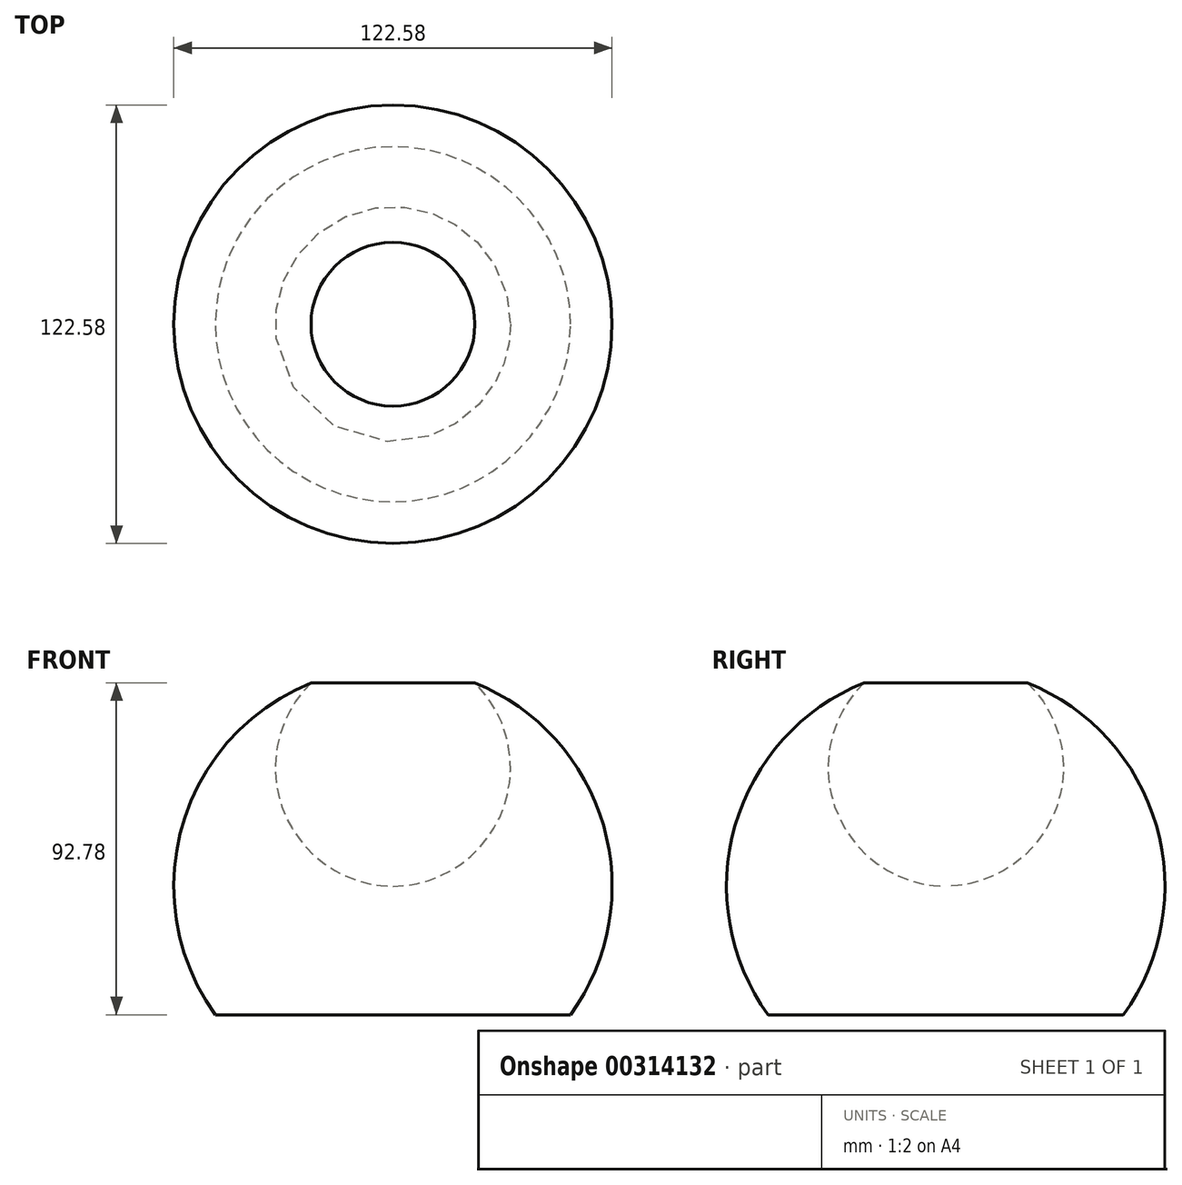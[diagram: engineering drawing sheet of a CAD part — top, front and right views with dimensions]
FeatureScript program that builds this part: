
annotation { "Feature Type Name" : "Feature", "Feature Type Description" : "" }
export const myFeature = defineFeature(function(context is Context, id is Id, definition is map)
    precondition{}
    {
        {
            var Q0;
            Q0=qCreatedBy(makeId("Front.planeOp"),FACE);
            var sketch = newSketch(context, id + "F0", { "sketchPlane" : qUnion([Q0])});
            skArc(sketch, "E0", {"start": v(49.65, -35.93) * mm, "mid": v(58.89, 16.98) * mm, "end": v(22.9, 56.85) * mm});
            skLineSegment(sketch, "E1", {"start": v(-49.65, -35.93) * mm, "end": v(49.65, -35.93) * mm});
            skLineSegment(sketch, "E2", {"start": v(0, -35.93) * mm, "end": v(0, 67.72) * mm});
            skArc(sketch, "E3", {"start": v(-23.82, 56.47) * mm, "mid": v(0, 0) * mm, "end": v(22.9, 56.85) * mm});
            skArc(sketch, "E4.trimOffspring", {"start": v(-23.82, 56.47) * mm, "mid": v(-59.02, 16.5) * mm, "end": v(-49.65, -35.93) * mm});
            skSolve(sketch);
        }
        {
            var Q0;
            {var subQ0=sQuery(id+"F0.wireOp",EDGE,"E1");var subQ1=sQuery(id+"F0.wireOp",EDGE,"E0");var subQ2=makeQuery(id+"F0.imprint","INTERSECT",VERTEX,{"disambiguationData":[OD(1.0)],"derivedFrom":[subQ1,subQ0]});Q0=makeQuery(id+"F0.imprint","IMPRINT",FACE,{"disambiguationData":[TD([[makeQuery(id+"F0.imprint","IMPRINT",EDGE,{"disambiguationData":[TD([[subQ2,1.0]])],"derivedFrom":subQ1}),1.0]])]});}
            var Q1;
            Q1=sQuery(id+"F0.wireOp",EDGE,"E2");
            revolve(context, id + "F1", {"entities" : qUnion([Q0]), "axis" : qUnion([Q1]), "revolveType" : RevolveType.FULL});
        }
    });
